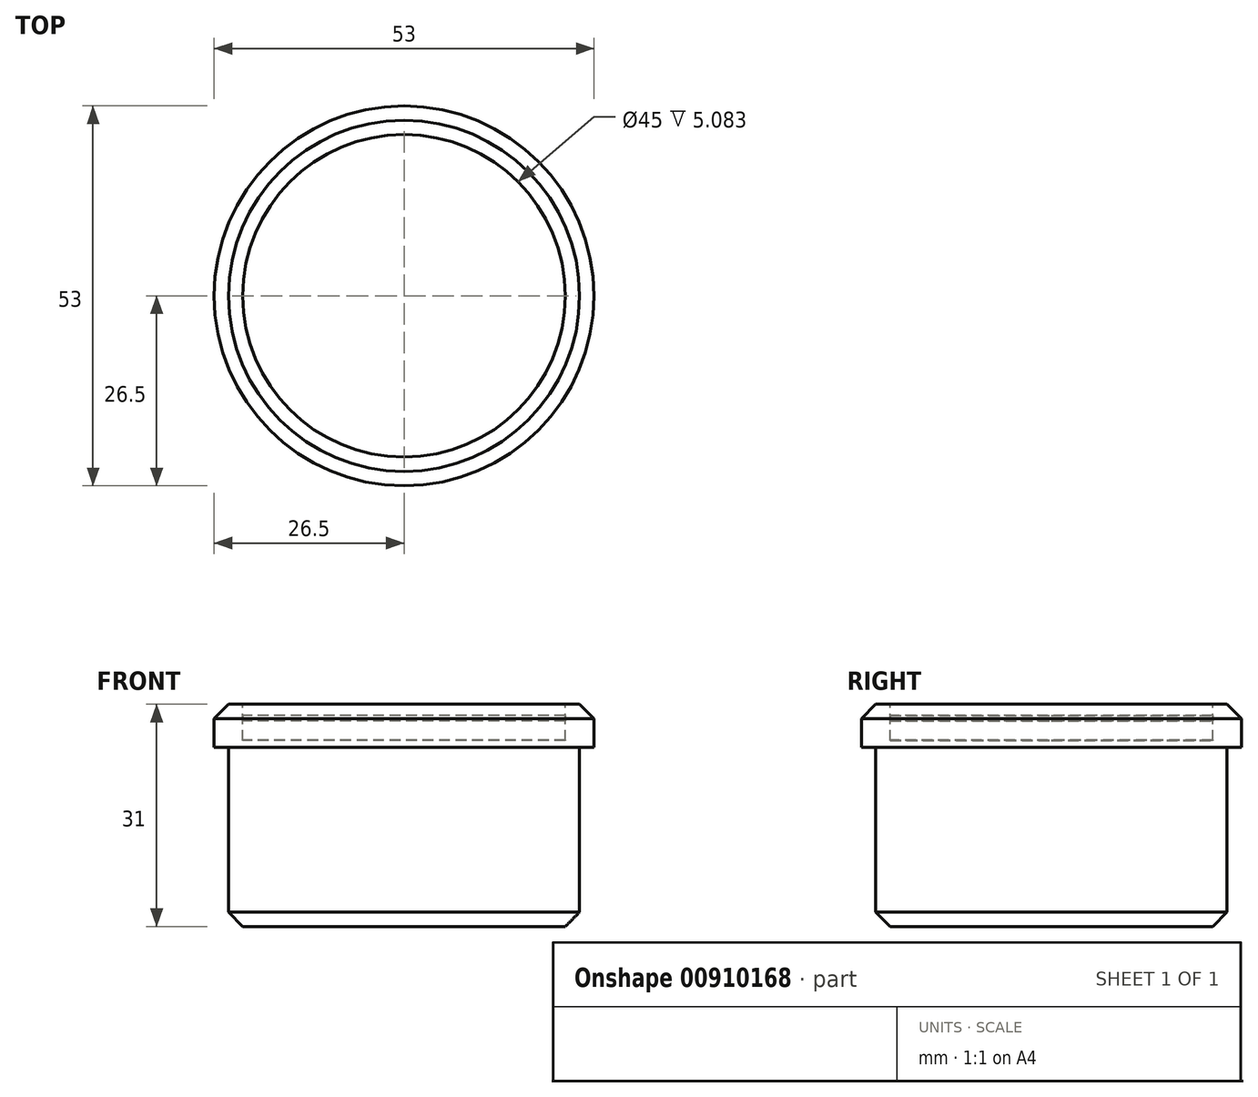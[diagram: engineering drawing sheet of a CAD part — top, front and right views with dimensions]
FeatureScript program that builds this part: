
annotation { "Feature Type Name" : "Feature", "Feature Type Description" : "" }
export const myFeature = defineFeature(function(context is Context, id is Id, definition is map)
    precondition{}
    {
        {
            var Q0;
            Q0=qCreatedBy(makeId("Front.planeOp"),FACE);
            var sketch = newSketch(context, id + "F0", { "sketchPlane" : qUnion([Q0])});
            skLineSegment(sketch, "E0", {"start": v(0, -25) * mm, "end": v(22.5, -25) * mm});
            skLineSegment(sketch, "E1", {"start": v(24.5, -23) * mm, "end": v(24.5, 0) * mm});
            skLineSegment(sketch, "E2", {"start": v(24.5, 0) * mm, "end": v(26.5, 0) * mm});
            skLineSegment(sketch, "E3", {"start": v(26.5, 0) * mm, "end": v(26.5, 4) * mm});
            skLineSegment(sketch, "E4", {"start": v(26.5, 4) * mm, "end": v(24.5, 6) * mm});
            skLineSegment(sketch, "E5", {"start": v(24.5, 6) * mm, "end": v(0, 6) * mm});
            skLineSegment(sketch, "E6", {"start": v(0, 6) * mm, "end": v(0, -25) * mm});
            skLineSegment(sketch, "E7", {"start": v(24.5, -23) * mm, "end": v(22.5, -25) * mm});
            skSolve(sketch);
        }
        {
            var Q0;
            Q0=makeQuery(id+"F0.imprint","IMPRINT",FACE,{"disambiguationData":[TD([[makeQuery(id+"F0.imprint","IMPRINT",EDGE,{"derivedFrom":sQuery(id+"F0.wireOp",EDGE,"E0")}),1.0]])]});
            var Q1;
            Q1=sQuery(id+"F0.wireOp",EDGE,"E6");
            revolve(context, id + "F1", {"surfaceOperationType" : NewSurfaceOperationType.NEW, "entities" : qUnion([Q0]), "axis" : qUnion([Q1]), "revolveType" : RevolveType.FULL});
        }
        {
            var Q0;
            Q0=makeQuery(id+"F1.opRevolve","SWEPT_FACE",FACE,{"disambiguationData":[OSD([sQuery(id+"F0.wireOp",EDGE,"E5")])]});
            var sketch = newSketch(context, id + "F2", { "sketchPlane" : qUnion([Q0])});
            skCircle(sketch, "E8", {"center": v(0, 0) * mm, "radius": 22.5 * mm});
            skSolve(sketch);
        }
        {
            var Q0;
            Q0=makeQuery(id+"F2.imprint","IMPRINT",FACE,{"disambiguationData":[TD([[makeQuery(id+"F2.imprint","IMPRINT",EDGE,{"derivedFrom":sQuery(id+"F2.wireOp",EDGE,"E8")}),1.0]])]});
            extrude(context, id + "F3", {"entities" : qUnion([Q0]), "operationType" : NewBodyOperationType.REMOVE, "oppositeDirection" : true, "depth" : 5.08 * mm, "offsetDistance" : 25 * mm});
        }
        {
            var Q0;
            Q0=makeQuery(id+"F3.boolean.opBoolean","COPY",FACE,{"derivedFrom":makeQuery(id+"F3.opExtrude","CAP_FACE",FACE,{"disambiguationData":[OSD([sQuery(id+"F2.wireOp",EDGE,"E8")])],"isStart":false})});
            var sketch = newSketch(context, id + "F4", { "sketchPlane" : qUnion([Q0])});
            skCircle(sketch, "E9", {"center": v(0, 0) * mm, "radius": 22.5 * mm});
            skSolve(sketch);
        }
        {
            var Q0;
            Q0=makeQuery(id+"F4.imprint","IMPRINT",FACE,{"disambiguationData":[TD([[makeQuery(id+"F4.imprint","IMPRINT",EDGE,{"derivedFrom":sQuery(id+"F4.wireOp",EDGE,"E9")}),1.0]])]});
            var Q1;
            Q1=sQuery(id+"F4.wireOp",EDGE,"E9");
            extrude(context, id + "F5", {"entities" : qUnion([Q0]), "surfaceEntities" : qUnion([Q1]), "depth" : 0.1 * mm, "offsetDistance" : 25 * mm});
        }
        {
            var Q0;
            Q0=makeQuery(id+"F5.opExtrude","CAP_FACE",FACE,{"disambiguationData":[OSD([sQuery(id+"F4.wireOp",EDGE,"E9")])],"isStart":false});
            cPlane(context, id + "F6", {"entities" : qUnion([Q0]), "cplaneType" : CPlaneType.OFFSET, "offset" : 2.65 * mm, "width" : 150 * mm, "height" : 150 * mm});
        }
        {
            var Q0;
            Q0=qCreatedBy(id+"F6.planeOp",FACE);
            var sketch = newSketch(context, id + "F7", { "sketchPlane" : qUnion([Q0])});
            skCircle(sketch, "E10", {"center": v(0, 0) * mm, "radius": 22.5 * mm});
            skSolve(sketch);
        }
        {
            var Q0;
            Q0 = qSketchRegion(id + "F7", true);
            extrude(context, id + "F8", {"entities" : qUnion([Q0]), "depth" : 0.75 * mm, "offsetDistance" : 25 * mm});
        }
    });
